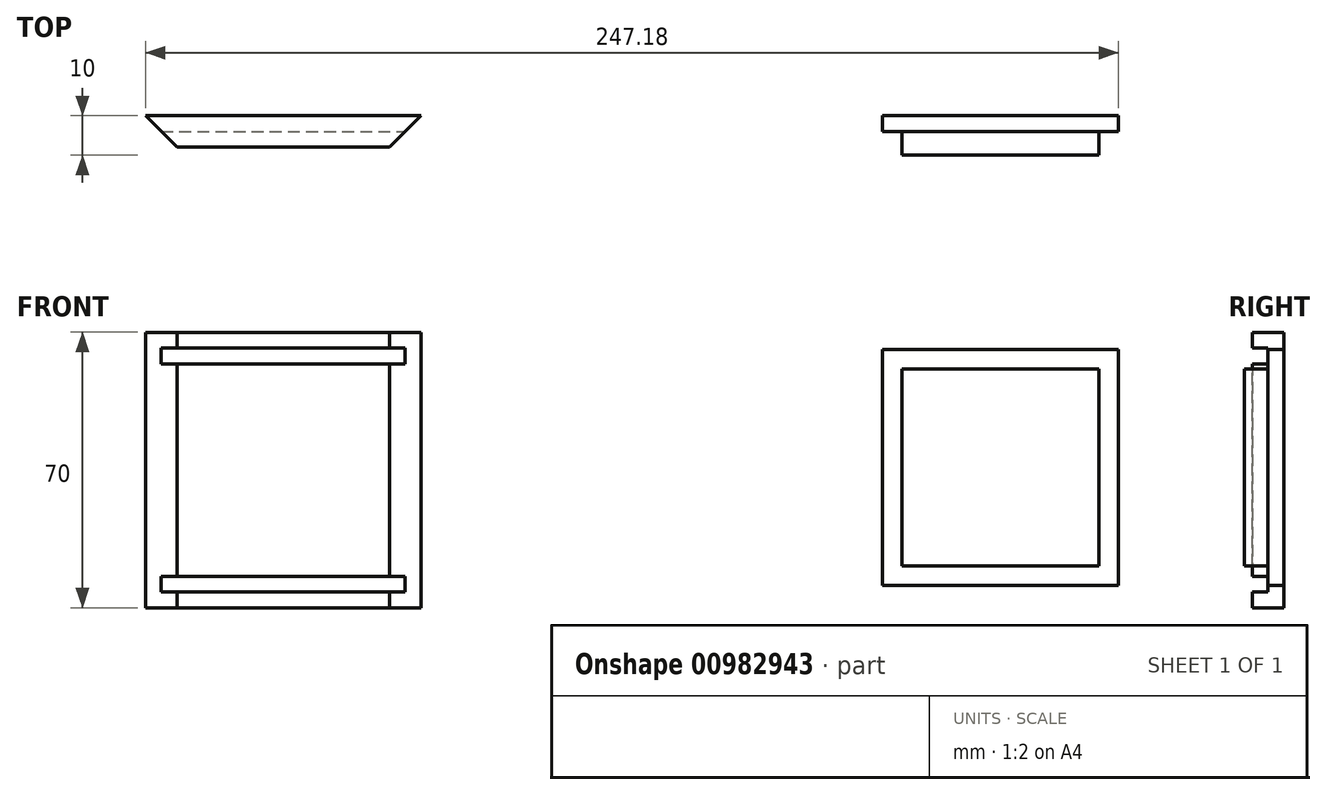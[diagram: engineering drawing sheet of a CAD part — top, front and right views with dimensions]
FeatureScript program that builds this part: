
annotation { "Feature Type Name" : "Feature", "Feature Type Description" : "" }
export const myFeature = defineFeature(function(context is Context, id is Id, definition is map)
    precondition{}
    {
        {
            var Q0;
            Q0=qCreatedBy(makeId("Front.planeOp"),FACE);
            var sketch = newSketch(context, id + "F0", { "sketchPlane" : qUnion([Q0])});
            skLineSegment(sketch, "E0.bottom", {"start": v(-1059.47, -27.27) * mm, "end": v(-989.47, -27.27) * mm});
            skLineSegment(sketch, "E0.top", {"start": v(-1059.47, -97.27) * mm, "end": v(-989.47, -97.27) * mm});
            skLineSegment(sketch, "E0.left", {"start": v(-1059.47, -27.27) * mm, "end": v(-1059.47, -97.27) * mm});
            skLineSegment(sketch, "E0.right", {"start": v(-989.47, -27.27) * mm, "end": v(-989.47, -97.27) * mm});
            skSolve(sketch);
        }
        {
            var Q0;
            Q0=makeQuery(id+"F0.imprint","IMPRINT",FACE,{"disambiguationData":[TD([[makeQuery(id+"F0.imprint","IMPRINT",EDGE,{"derivedFrom":sQuery(id+"F0.wireOp",EDGE,"E0.bottom")}),-1.0]])]});
            extrude(context, id + "F1", {"entities" : qUnion([Q0]), "depth" : 8 * mm, "offsetDistance" : 25 * mm});
        }
        {
            var Q0;
            Q0=makeQuery(id+"F1.opExtrude","CAP_FACE",FACE,{"disambiguationData":[OSD([sQuery(id+"F0.wireOp",EDGE,"E0.bottom"),sQuery(id+"F0.wireOp",EDGE,"E0.top"),sQuery(id+"F0.wireOp",EDGE,"E0.left"),sQuery(id+"F0.wireOp",EDGE,"E0.right")])],"isStart":false});
            var sketch = newSketch(context, id + "F2", { "sketchPlane" : qUnion([Q0])});
            skLineSegment(sketch, "E1.bottom", {"start": v(-1059.47, -31.27) * mm, "end": v(-989.47, -31.27) * mm});
            skLineSegment(sketch, "E1.top", {"start": v(-1059.47, -35.27) * mm, "end": v(-989.47, -35.27) * mm});
            skLineSegment(sketch, "E1.left", {"start": v(-1059.47, -31.27) * mm, "end": v(-1059.47, -35.27) * mm});
            skLineSegment(sketch, "E1.right", {"start": v(-989.47, -31.27) * mm, "end": v(-989.47, -35.27) * mm});
            skLineSegment(sketch, "E2.bottom", {"start": v(-1059.47, -89.27) * mm, "end": v(-989.47, -89.27) * mm});
            skLineSegment(sketch, "E2.top", {"start": v(-1059.47, -93.27) * mm, "end": v(-989.47, -93.27) * mm});
            skLineSegment(sketch, "E2.left", {"start": v(-1059.47, -89.27) * mm, "end": v(-1059.47, -93.27) * mm});
            skLineSegment(sketch, "E2.right", {"start": v(-989.47, -89.27) * mm, "end": v(-989.47, -93.27) * mm});
            skSolve(sketch);
        }
        {
            var Q0;
            Q0 = qSketchRegion(id + "F2", true);
            extrude(context, id + "F3", {"entities" : qUnion([Q0]), "operationType" : NewBodyOperationType.REMOVE, "oppositeDirection" : true, "depth" : 4 * mm, "offsetDistance" : 25 * mm});
        }
        {
            var Q0;
            {var subQ0=sQuery(id+"F0.wireOp",EDGE,"E0.right");Q0=makeQuery(id+"F3.boolean.opBoolean","SPLIT",EDGE,{"disambiguationData":[TD([makeQuery(id+"F3.opExtrude","SWEPT_FACE",FACE,{"disambiguationData":[OSD([sQuery(id+"F2.wireOp",EDGE,"E1.top")])]})])],"derivedFrom":makeQuery(id+"F1.opExtrude","CAP_EDGE",EDGE,{"disambiguationData":[OSD([subQ0])],"isStart":false})});}
            var Q1;
            {var subQ0=sQuery(id+"F0.wireOp",EDGE,"E0.left");Q1=makeQuery(id+"F3.boolean.opBoolean","SPLIT",EDGE,{"disambiguationData":[TD([makeQuery(id+"F3.opExtrude","SWEPT_FACE",FACE,{"disambiguationData":[OSD([sQuery(id+"F2.wireOp",EDGE,"E1.top")])]})])],"derivedFrom":makeQuery(id+"F1.opExtrude","CAP_EDGE",EDGE,{"disambiguationData":[OSD([subQ0])],"isStart":false})});}
            chamfer(context, id + "F4", {"entities" : qUnion([Q0, Q1]), "width" : 8 * mm, "tangentPropagation" : true});
        }
        {
            var Q0;
            Q0=qCreatedBy(makeId("Front.planeOp"),FACE);
            var sketch = newSketch(context, id + "F5", { "sketchPlane" : qUnion([Q0])});
            skLineSegment(sketch, "E3.bottom", {"start": v(-872.29, -31.62) * mm, "end": v(-812.29, -31.62) * mm});
            skLineSegment(sketch, "E3.top", {"start": v(-872.29, -91.62) * mm, "end": v(-812.29, -91.62) * mm});
            skLineSegment(sketch, "E3.left", {"start": v(-872.29, -31.62) * mm, "end": v(-872.29, -91.62) * mm});
            skLineSegment(sketch, "E3.right", {"start": v(-812.29, -31.62) * mm, "end": v(-812.29, -91.62) * mm});
            skSolve(sketch);
        }
        {
            var Q0;
            Q0 = qSketchRegion(id + "F5", true);
            extrude(context, id + "F6", {"entities" : qUnion([Q0]), "depth" : 10 * mm, "offsetDistance" : 25 * mm});
        }
        {
            var Q0;
            Q0=makeQuery(id+"F6.opExtrude","CAP_FACE",FACE,{"disambiguationData":[OSD([sQuery(id+"F5.wireOp",EDGE,"E3.bottom"),sQuery(id+"F5.wireOp",EDGE,"E3.top"),sQuery(id+"F5.wireOp",EDGE,"E3.left"),sQuery(id+"F5.wireOp",EDGE,"E3.right")])],"isStart":false});
            var sketch = newSketch(context, id + "F7", { "sketchPlane" : qUnion([Q0])});
            skLineSegment(sketch, "E4.bottom", {"start": v(-817.29, -36.62) * mm, "end": v(-867.29, -36.62) * mm});
            skLineSegment(sketch, "E4.top", {"start": v(-817.29, -86.62) * mm, "end": v(-867.29, -86.62) * mm});
            skLineSegment(sketch, "E4.left", {"start": v(-817.29, -36.62) * mm, "end": v(-817.29, -86.62) * mm});
            skLineSegment(sketch, "E4.right", {"start": v(-867.29, -36.62) * mm, "end": v(-867.29, -86.62) * mm});
            skPoint(sketch, "E4.middle", {"position": v(-842.29, -61.62) * mm});
            skPoint(sketch, "E4.middle.positionSnap0", {"position": v(-812.29, -61.62) * mm});
            skPoint(sketch, "E4.middle.positionSnap1", {"position": v(-842.29, -31.62) * mm});
            skPoint(sketch, "E4.centerSnap0", {"position": v(-812.29, -61.62) * mm});
            skPoint(sketch, "E4.centerSnap1", {"position": v(-842.29, -31.62) * mm});
            skSolve(sketch);
        }
        {
            var Q0;
            Q0=makeQuery(id+"F7.imprint","IMPRINT",FACE,{"disambiguationData":[TD([[makeQuery(id+"F7.imprint","IMPRINT",EDGE,{"derivedFrom":sQuery(id+"F7.wireOp",EDGE,"E4.bottom")}),-1.0]])]});
            extrude(context, id + "F8", {"entities" : qUnion([Q0]), "operationType" : NewBodyOperationType.REMOVE, "oppositeDirection" : true, "depth" : 6 * mm, "offsetDistance" : 25 * mm});
        }
    });
